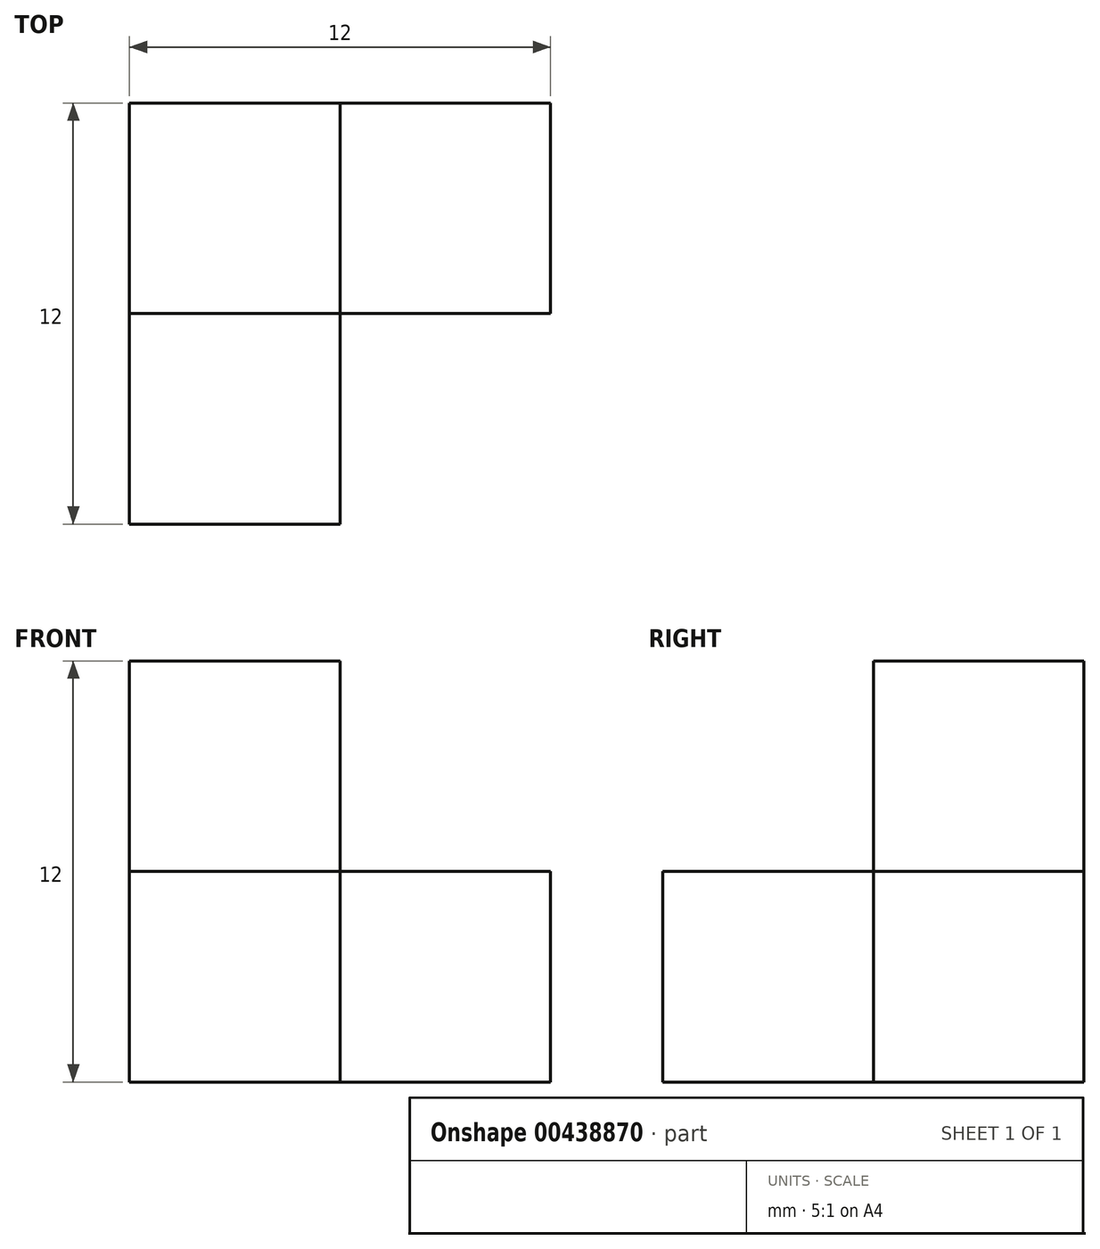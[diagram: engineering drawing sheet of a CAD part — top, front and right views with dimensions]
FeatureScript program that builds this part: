
annotation { "Feature Type Name" : "Feature", "Feature Type Description" : "" }
export const myFeature = defineFeature(function(context is Context, id is Id, definition is map)
    precondition{}
    {
        {
            var Q0;
            Q0=qCreatedBy(makeId("Top.planeOp"),FACE);
            var sketch = newSketch(context, id + "F0", { "sketchPlane" : qUnion([Q0])});
            skLineSegment(sketch, "E0", {"start": v(0, 0) * mm, "end": v(-6, 0) * mm});
            skLineSegment(sketch, "E1", {"start": v(-6, 0) * mm, "end": v(-6, 6) * mm});
            skLineSegment(sketch, "E2", {"start": v(-6, 6) * mm, "end": v(0, 6) * mm});
            skLineSegment(sketch, "E3", {"start": v(0, 6) * mm, "end": v(0, -0.37) * mm});
            skSolve(sketch);
        }
        {
            var Q0;
            {var subQ0=sQuery(id+"F0.wireOp",EDGE,"E0");Q0=makeQuery(id+"F0.imprint","IMPRINT",FACE,{"disambiguationData":[TD([[makeQuery(id+"F0.imprint","IMPRINT",EDGE,{"derivedFrom":subQ0}),-1.0]])]});}
            extrude(context, id + "F1", {"entities" : qUnion([Q0]), "depth" : 6 * mm});
        }
        {
            var Q0;
            Q0=qCreatedBy(makeId("Top.planeOp"),FACE);
            var sketch = newSketch(context, id + "F2", { "sketchPlane" : qUnion([Q0])});
            skLineSegment(sketch, "E4", {"start": v(0, 3.03) * mm, "end": v(6, 3.03) * mm});
            skSolve(sketch);
        }
        {
            var Q0;
            Q0=makeQuery(id+"F1.opExtrude","SWEPT_FACE",FACE,{"disambiguationData":[OSD([sQuery(id+"F0.wireOp",EDGE,"E3")])]});
            var Q1;
            Q1=sQuery(id+"F2.wireOp",EDGE,"E4");
            sweep(context, id + "F3", {"operationType" : NewBodyOperationType.ADD, "profiles" : qUnion([Q0]), "path" : qUnion([Q1])});
        }
        {
            var Q0;
            Q0=qCreatedBy(makeId("Top.planeOp"),FACE);
            cPlane(context, id + "F4", {"entities" : qUnion([Q0]), "cplaneType" : CPlaneType.OFFSET, "offset" : 6 * mm, "width" : 150 * mm, "height" : 150 * mm});
        }
        {
            var Q0;
            Q0=qCreatedBy(id+"F4.planeOp",FACE);
            var sketch = newSketch(context, id + "F5", { "sketchPlane" : qUnion([Q0])});
            skLineSegment(sketch, "E5", {"start": v(0, 0) * mm, "end": v(0, 6) * mm});
            skLineSegment(sketch, "E6", {"start": v(0, 6) * mm, "end": v(-6, 6) * mm});
            skLineSegment(sketch, "E7", {"start": v(-6, 6) * mm, "end": v(-6, 0) * mm});
            skLineSegment(sketch, "E8", {"start": v(-6, 0) * mm, "end": v(0, 0) * mm});
            skSolve(sketch);
        }
        {
            var Q0;
            Q0 = qSketchRegion(id + "F5", true);
            extrude(context, id + "F6", {"entities" : qUnion([Q0]), "operationType" : NewBodyOperationType.ADD, "depth" : 6 * mm});
        }
        {
            var Q0;
            Q0=qCreatedBy(makeId("Top.planeOp"),FACE);
            var sketch = newSketch(context, id + "F7", { "sketchPlane" : qUnion([Q0])});
            skLineSegment(sketch, "E9", {"start": v(0, 0) * mm, "end": v(-6, 0) * mm});
            skLineSegment(sketch, "E10", {"start": v(-6, 0) * mm, "end": v(-6, -6) * mm});
            skLineSegment(sketch, "E11", {"start": v(-6, -6) * mm, "end": v(0, -6) * mm});
            skLineSegment(sketch, "E12", {"start": v(0, -6) * mm, "end": v(0, 0) * mm});
            skSolve(sketch);
        }
        {
            var Q0;
            Q0=makeQuery(id+"F7.imprint","IMPRINT",FACE,{"disambiguationData":[TD([[makeQuery(id+"F7.imprint","IMPRINT",EDGE,{"derivedFrom":sQuery(id+"F7.wireOp",EDGE,"E9")}),1.0]])]});
            extrude(context, id + "F8", {"entities" : qUnion([Q0]), "operationType" : NewBodyOperationType.ADD, "depth" : 6 * mm});
        }
    });
